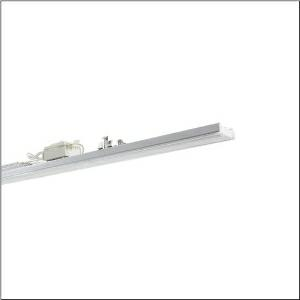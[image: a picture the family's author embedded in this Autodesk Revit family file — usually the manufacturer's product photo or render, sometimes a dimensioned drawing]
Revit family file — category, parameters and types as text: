
# Revit family: licross_r__11_recessed_ho_51te12dv4m2m3s4_7ec3
name_source: partatom
category: Lighting Fixtures
units: mm (PartAtom-declared; Revit-internal decimal feet)

## family parameters
Cut with Voids When Loaded = No
Host = Face
Light Source = No
Part Type = Normal
Room Calculation Point = No
Round Connector Dimension = Use Diameter
Shared = No

## types (1)
- --- (1 x LED, 1010 lm, 5.9 W, 4000K)
    Apparent Load = 6 VA
    CIE Flux Codes = 66 91 98 100 100
    Color Rendering = 80
    Color Temperature = 4000K
    Default Elevation = 1800 mm
    Description = Licross® 11 Recessed HO, luminaire insert, of sheet steel, galvanised, coil coated, white, length: 2.250mm, width: 66mm, height: 67mm, LED rated luminous flux: 27.150lm, light colour: 840, control gear: DALI 2, with plug, 6-pole, with phase selection, for trunking rail, 9 or 11-core, mains connection: 220..240V, AC, 50/60Hz, rated input power: 154W, for trunking rail, 9-/11-core, internal wiring halogen-free, for emergency light function, converter,control gear: single battery element, battery: LiFePO4, 9Ah, primary optical cover: cover, of PMMA, light emission: direct distribution, primary light characteristic: symmetric, protection rating (complete): IP54, insulation class (complete): insulation class I (protective earthing), certification: CE, UKCA, protection symbol: D if used in an environment with non-conductive dust loads with corresponding accessories, impact resistance: IK06, permissible ambient temperature for indoor applications: +5..+35°C, standard: EN 60598-2-22, LABS conformity tested according to VDMA 24364:2018-05, reducing of maximum allowable ambient temperature of 5°C with ceiling mounting, corresponds to IFS (International Featured Standards) requirements for safety and quality in the food industry, packaging unit: 1 piece
    Height = 58 mm
    Lamp = 1 x LED
    Lamp Light Flux = 1010 lm
    Lamp Power = 5.9 W
    Lamp count = 1
    Length = 2250 mm
    Luminous efficacy = 171 lm/W
    Manufacturer = Siteco
    ModVariant = No
    Model = 51TE12DV4M2M3S4
    Mounting Place = Ceiling
    Mounting Type = Pendant
    Number of Poles = 1
    OnlyDefault = Yes
    Power Factor = 1
    Product Name = Licross® 11 Recessed HO
    Product group = luminaire insert | ceiling pendant
    ProductGroupID = 902
    Protection Class = Protection class I
    Protection Degree = IP 54
    RLX_Detail_Level = 1
    RLX_Emergency_Light_Flux = 0 lm
    RLX_Emergency_Type = 0
    RLX_Emergency_Type_DB = No
    RlxData = <blob elided: 29893 chars, md5=d2eaaaf4>
    Socket = socket
    Standby Power = 0 W
    System Light Flux = 1010 lm
    System Power = 6 W
    Type Comments = : emergency light operation: 3 h
    Type Image = l_1296930.jpg
    URL = http://relux.com
    VarID = @adj_106279
    Voltage = 0 V
    Weight = 0.00 kg
    Width = 66 mm

## geometry (parser evidence)
native form markers: Blend x4, Sweep x10
no freeform markers — native parametric forms only
